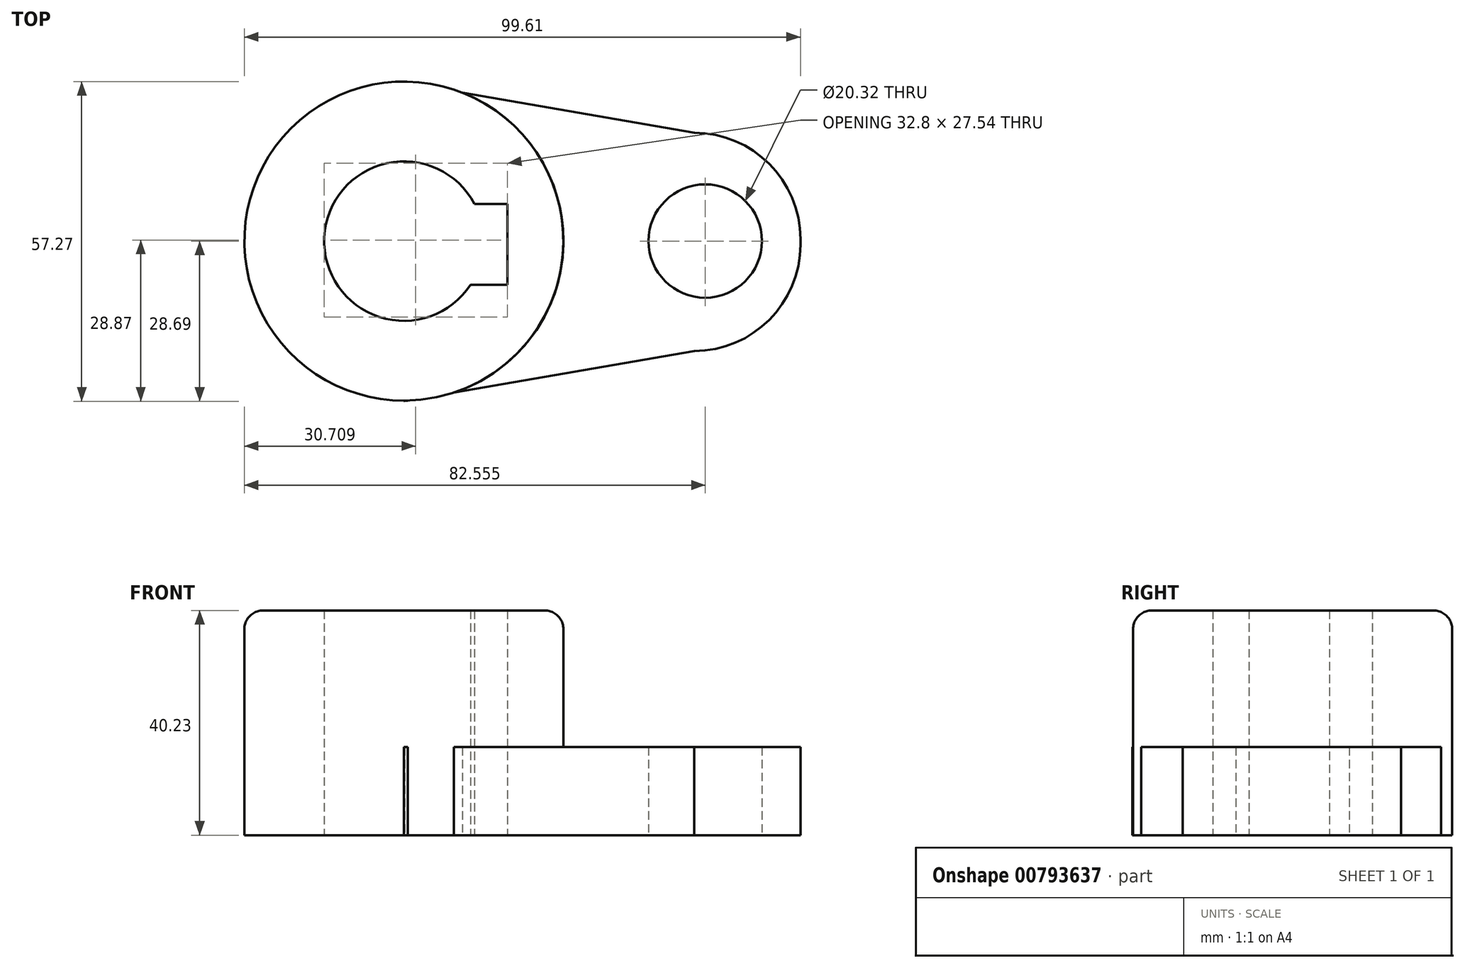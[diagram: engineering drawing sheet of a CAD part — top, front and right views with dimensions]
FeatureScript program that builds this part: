
annotation { "Feature Type Name" : "Feature", "Feature Type Description" : "" }
export const myFeature = defineFeature(function(context is Context, id is Id, definition is map)
    precondition{}
    {
        {
            var Q0;
            Q0=qCreatedBy(makeId("Top.planeOp"),FACE);
            var sketch = newSketch(context, id + "F0", { "sketchPlane" : qUnion([Q0])});
            skCircle(sketch, "E0", {"center": v(0, 0) * mm, "radius": 14.29 * mm});
            skLineSegment(sketch, "E1", {"start": v(-14.29, 0) * mm, "end": v(18.53, 0) * mm});
            skLineSegment(sketch, "E2.bottom", {"start": v(18.53, -7.8) * mm, "end": v(8.88, -7.8) * mm});
            skLineSegment(sketch, "E2.top", {"start": v(18.53, 6.63) * mm, "end": v(8.88, 6.63) * mm});
            skLineSegment(sketch, "E2.left", {"start": v(18.53, -7.8) * mm, "end": v(18.53, 6.63) * mm});
            skLineSegment(sketch, "E2.right", {"start": v(8.88, -7.8) * mm, "end": v(8.88, 6.63) * mm});
            skSolve(sketch);
        }
        {
            var Q0;
            Q0=qCreatedBy(makeId("Top.planeOp"),FACE);
            var sketch = newSketch(context, id + "F1", { "sketchPlane" : qUnion([Q0])});
            skCircle(sketch, "E3", {"center": v(0, 0) * mm, "radius": 28.58 * mm});
            skSolve(sketch);
        }
        {
            var Q0;
            Q0 = qSketchRegion(id + "F1", true);
            extrude(context, id + "F2", {"entities" : qUnion([Q0]), "depth" : 40.23 * mm, "offsetDistance" : 25.4 * mm});
        }
        {
            var Q0;
            Q0=makeQuery(id+"F2.opExtrude","CAP_FACE",FACE,{"disambiguationData":[OSD([sQuery(id+"F1.wireOp",EDGE,"E3")])],"isStart":false});
            fillet(context, id + "F3", {"entities" : qUnion([Q0]), "radius" : 3.3 * mm, "tangentPropagation" : true, "allowEdgeOverflow" : false});
        }
        {
            var Q0;
            Q0 = qSketchRegion(id + "F0", true);
            extrude(context, id + "F4", {"entities" : qUnion([Q0]), "operationType" : NewBodyOperationType.REMOVE, "depth" : 40.23 * mm, "offsetDistance" : 25.4 * mm});
        }
        {
            var Q0;
            Q0=qCreatedBy(makeId("Top.planeOp"),FACE);
            var sketch = newSketch(context, id + "F5", { "sketchPlane" : qUnion([Q0])});
            skCircle(sketch, "E4", {"center": v(53.98, 0) * mm, "radius": 10.16 * mm});
            skSolve(sketch);
        }
        {
            var Q0;
            Q0=qCreatedBy(makeId("Top.planeOp"),FACE);
            var sketch = newSketch(context, id + "F6", { "sketchPlane" : qUnion([Q0])});
            skLineSegment(sketch, "E5.bottom", {"start": v(37, 19.4) * mm, "end": v(51.98, 19.4) * mm});
            skLineSegment(sketch, "E5.top", {"start": v(37, -19.69) * mm, "end": v(51.98, -19.69) * mm});
            skLineSegment(sketch, "E5.left", {"start": v(37, 19.4) * mm, "end": v(37, -19.69) * mm});
            skLineSegment(sketch, "E5.right", {"start": v(71.03, 0.35) * mm, "end": v(71.03, -0.64) * mm});
            skPoint(sketch, "E6.visualSharp", {"position": v(71.03, 19.4) * mm});
            skArc(sketch, "E6.filletArc", {"start": v(71.03, 0.35) * mm, "mid": v(65.45, 13.83) * mm, "end": v(51.98, 19.4) * mm});
            skPoint(sketch, "E7.visualSharp", {"position": v(71.03, -19.69) * mm});
            skArc(sketch, "E7.filletArc", {"start": v(51.98, -19.69) * mm, "mid": v(65.45, -14.1) * mm, "end": v(71.03, -0.64) * mm});
            skLineSegment(sketch, "E8", {"start": v(51.98, -19.69) * mm, "end": v(0, -28.69) * mm});
            skLineSegment(sketch, "E9", {"start": v(0, -28.69) * mm, "end": v(21.52, -8.72) * mm});
            skLineSegment(sketch, "E10", {"start": v(21.52, -8.72) * mm, "end": v(21.52, 10.12) * mm});
            skLineSegment(sketch, "E11", {"start": v(21.52, 10.12) * mm, "end": v(0, 28.4) * mm});
            skLineSegment(sketch, "E12", {"start": v(0, 28.4) * mm, "end": v(51.98, 19.4) * mm});
            skSolve(sketch);
        }
        {
            var Q0;
            Q0 = qSketchRegion(id + "F6", true);
            extrude(context, id + "F7", {"entities" : qUnion([Q0]), "operationType" : NewBodyOperationType.ADD, "depth" : 15.77 * mm, "offsetDistance" : 25.4 * mm});
        }
        {
            var Q0;
            Q0=makeQuery(id+"F5.imprint","IMPRINT",FACE,{"disambiguationData":[TD([[makeQuery(id+"F5.imprint","IMPRINT",EDGE,{"derivedFrom":sQuery(id+"F5.wireOp",EDGE,"E4")}),1.0]])]});
            extrude(context, id + "F8", {"entities" : qUnion([Q0]), "operationType" : NewBodyOperationType.REMOVE, "depth" : 25.4 * mm, "offsetDistance" : 25.4 * mm});
        }
    });
